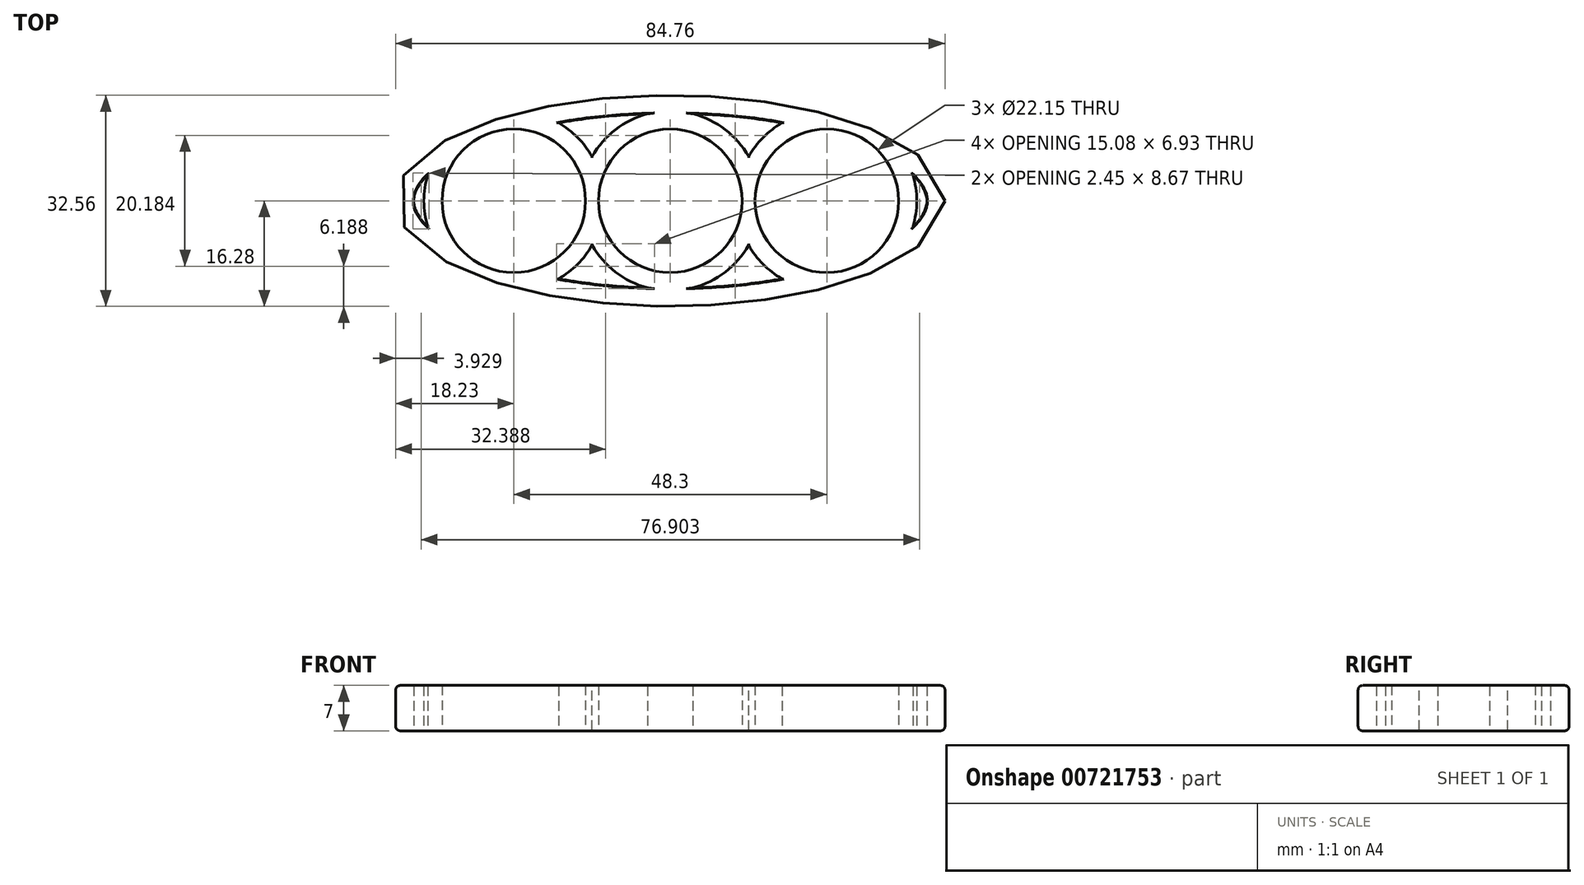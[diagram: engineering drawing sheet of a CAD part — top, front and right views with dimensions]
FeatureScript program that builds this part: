
annotation { "Feature Type Name" : "Feature", "Feature Type Description" : "" }
export const myFeature = defineFeature(function(context is Context, id is Id, definition is map)
    precondition{}
    {
        {
            var Q0;
            Q0=qCreatedBy(makeId("Top.planeOp"),FACE);
            var sketch = newSketch(context, id + "F0", { "sketchPlane" : qUnion([Q0])});
            skCircle(sketch, "E0", {"center": v(0, 0) * mm, "radius": 11.07 * mm});
            skCircle(sketch, "E1", {"center": v(24.15, 0) * mm, "radius": 11.07 * mm});
            skCircle(sketch, "E2", {"center": v(-24.15, 0) * mm, "radius": 11.07 * mm});
            skSolve(sketch);
        }
        {
            var Q0;
            Q0=qCreatedBy(makeId("Top.planeOp"),FACE);
            var sketch = newSketch(context, id + "F1", { "sketchPlane" : qUnion([Q0])});
            skEllipse(sketch, "E3", {"center": v(0, 0) * mm, "majorRadius": 42.38 * mm, "minorRadius": 16.28 * mm, "majorAxis": v(1, 0)});
            skSolve(sketch);
        }
        {
            var Q0;
            Q0=makeQuery(id+"F1.imprint","IMPRINT",FACE,{"disambiguationData":[TD([[makeQuery(id+"F1.imprint","IMPRINT",EDGE,{"derivedFrom":sQuery(id+"F1.wireOp",EDGE,"E3")}),1.0]])]});
            extrude(context, id + "F2", {"entities" : qUnion([Q0]), "depth" : 7 * mm, "offsetDistance" : 25 * mm});
        }
        {
            var Q0;
            Q0=makeQuery(id+"F0.imprint","IMPRINT",FACE,{"disambiguationData":[TD([[makeQuery(id+"F0.imprint","IMPRINT",EDGE,{"derivedFrom":sQuery(id+"F0.wireOp",EDGE,"E2")}),1.0]])]});
            var Q1;
            Q1=makeQuery(id+"F0.imprint","IMPRINT",FACE,{"disambiguationData":[TD([[makeQuery(id+"F0.imprint","IMPRINT",EDGE,{"derivedFrom":sQuery(id+"F0.wireOp",EDGE,"E0")}),1.0]])]});
            var Q2;
            Q2=makeQuery(id+"F0.imprint","IMPRINT",FACE,{"disambiguationData":[TD([[makeQuery(id+"F0.imprint","IMPRINT",EDGE,{"derivedFrom":sQuery(id+"F0.wireOp",EDGE,"E1")}),1.0]])]});
            extrude(context, id + "F3", {"entities" : qUnion([Q0, Q1, Q2]), "operationType" : NewBodyOperationType.REMOVE, "depth" : 25.5 * mm, "offsetDistance" : 25 * mm});
        }
        {
            var Q0;
            Q0=makeQuery(id+"F2.opExtrude","CAP_FACE",FACE,{"disambiguationData":[OSD([sQuery(id+"F1.wireOp",EDGE,"E3")])],"isStart":false});
            var Q1;
            Q1=makeQuery(id+"F2.opExtrude","CAP_FACE",FACE,{"disambiguationData":[OSD([sQuery(id+"F1.wireOp",EDGE,"E3")])],"isStart":true});
            shell(context, id + "F4", {"entities" : qUnion([Q0, Q1]), "thickness" : 2.8 * mm});
        }
        {
            var Q0;
            Q0=makeQuery(id+"F2.opExtrude","CAP_EDGE",EDGE,{"disambiguationData":[OSD([sQuery(id+"F1.wireOp",EDGE,"E3")])],"isStart":true});
            var Q1;
            Q1=makeQuery(id+"F2.opExtrude","CAP_EDGE",EDGE,{"disambiguationData":[OSD([sQuery(id+"F1.wireOp",EDGE,"E3")])],"isStart":false});
            fillet(context, id + "F5", {"entities" : qUnion([Q0, Q1]), "radius" : 0.7 * mm, "tangentPropagation" : true, "allowEdgeOverflow" : false});
        }
        {
            var Q0;
            {var subQ0=sQuery(id+"F1.wireOp",EDGE,"E3");Q0=makeQuery(id+"F4.opShell","OFFSET_EDGE",EDGE,{"disambiguationData":[OSD([subQ0]),TDD([makeQuery(id+"F2.opExtrude","CAP_EDGE",EDGE,{"disambiguationData":[OSD([subQ0])],"isStart":true})]),OD(1.0)]});}
            var Q1;
            Q1=makeQuery(id+"F4.opShell","OFFSET_EDGE",EDGE,{"disambiguationData":[OSD([sQuery(id+"F0.wireOp",EDGE,"E2")]),OD(0.0)]});
            var Q2;
            {var subQ0=sQuery(id+"F1.wireOp",EDGE,"E3");Q2=makeQuery(id+"F4.opShell","OFFSET_EDGE",EDGE,{"disambiguationData":[OSD([subQ0]),TDD([makeQuery(id+"F2.opExtrude","CAP_EDGE",EDGE,{"disambiguationData":[OSD([subQ0])],"isStart":true})]),OD(2.0)]});}
            var Q3;
            Q3=makeQuery(id+"F4.opShell","OFFSET_EDGE",EDGE,{"disambiguationData":[OSD([sQuery(id+"F0.wireOp",EDGE,"E2")]),OD(1.0)]});
            var Q4;
            Q4=makeQuery(id+"F4.opShell","OFFSET_EDGE",EDGE,{"disambiguationData":[OSD([sQuery(id+"F0.wireOp",EDGE,"E0")]),OD(0.0)]});
            var Q5;
            Q5=makeQuery(id+"F4.opShell","OFFSET_EDGE",EDGE,{"disambiguationData":[OSD([sQuery(id+"F0.wireOp",EDGE,"E0")]),OD(1.0)]});
            var Q6;
            {var subQ0=sQuery(id+"F1.wireOp",EDGE,"E3");Q6=makeQuery(id+"F4.opShell","OFFSET_EDGE",EDGE,{"disambiguationData":[OSD([subQ0]),TDD([makeQuery(id+"F2.opExtrude","CAP_EDGE",EDGE,{"disambiguationData":[OSD([subQ0])],"isStart":true})]),OD(3.0)]});}
            var Q7;
            Q7=makeQuery(id+"F4.opShell","OFFSET_EDGE",EDGE,{"disambiguationData":[OSD([sQuery(id+"F0.wireOp",EDGE,"E1")]),OD(1.0)]});
            var Q8;
            {var subQ0=sQuery(id+"F1.wireOp",EDGE,"E3");Q8=makeQuery(id+"F4.opShell","OFFSET_EDGE",EDGE,{"disambiguationData":[OSD([subQ0]),TDD([makeQuery(id+"F2.opExtrude","CAP_EDGE",EDGE,{"disambiguationData":[OSD([subQ0])],"isStart":true})]),OD(0.0)]});}
            var Q9;
            Q9=makeQuery(id+"F4.opShell","OFFSET_EDGE",EDGE,{"disambiguationData":[OSD([sQuery(id+"F0.wireOp",EDGE,"E1")]),OD(0.0)]});
            var Q10;
            Q10=makeQuery(id+"F4.opShell","OFFSET_EDGE",EDGE,{"disambiguationData":[OSD([sQuery(id+"F0.wireOp",EDGE,"E1")]),OD(2.0)]});
            var Q11;
            Q11=makeQuery(id+"F4.opShell","OFFSET_EDGE",EDGE,{"disambiguationData":[OSD([sQuery(id+"F0.wireOp",EDGE,"E0")]),OD(3.0)]});
            var Q12;
            {var subQ0=sQuery(id+"F1.wireOp",EDGE,"E3");Q12=makeQuery(id+"F4.opShell","OFFSET_EDGE",EDGE,{"disambiguationData":[OSD([subQ0]),TDD([makeQuery(id+"F2.opExtrude","CAP_EDGE",EDGE,{"disambiguationData":[OSD([subQ0])],"isStart":true})]),OD(5.0)]});}
            var Q13;
            Q13=makeQuery(id+"F4.opShell","OFFSET_EDGE",EDGE,{"disambiguationData":[OSD([sQuery(id+"F0.wireOp",EDGE,"E0")]),OD(2.0)]});
            var Q14;
            Q14=makeQuery(id+"F4.opShell","OFFSET_EDGE",EDGE,{"disambiguationData":[OSD([sQuery(id+"F0.wireOp",EDGE,"E2")]),OD(2.0)]});
            var Q15;
            {var subQ0=sQuery(id+"F1.wireOp",EDGE,"E3");Q15=makeQuery(id+"F4.opShell","OFFSET_EDGE",EDGE,{"disambiguationData":[OSD([subQ0]),TDD([makeQuery(id+"F2.opExtrude","CAP_EDGE",EDGE,{"disambiguationData":[OSD([subQ0])],"isStart":true})]),OD(4.0)]});}
            var Q16;
            {var subQ0=sQuery(id+"F1.wireOp",EDGE,"E3");Q16=makeQuery(id+"F4.opShell","OFFSET_EDGE",EDGE,{"disambiguationData":[OSD([subQ0]),TDD([makeQuery(id+"F2.opExtrude","CAP_EDGE",EDGE,{"disambiguationData":[OSD([subQ0])],"isStart":false})]),OD(4.0)]});}
            var Q17;
            Q17=makeQuery(id+"F4.opShell","OFFSET_EDGE",EDGE,{"disambiguationData":[OSD([sQuery(id+"F0.wireOp",EDGE,"E2"),sQuery(id+"F1.wireOp",EDGE,"E3")]),OD(2.0)]});
            var Q18;
            Q18=makeQuery(id+"F4.opShell","OFFSET_EDGE",EDGE,{"disambiguationData":[OSD([sQuery(id+"F0.wireOp",EDGE,"E0"),sQuery(id+"F1.wireOp",EDGE,"E3")]),OD(2.0)]});
            var Q19;
            {var subQ0=sQuery(id+"F1.wireOp",EDGE,"E3");Q19=makeQuery(id+"F4.opShell","OFFSET_EDGE",EDGE,{"disambiguationData":[OSD([subQ0]),TDD([makeQuery(id+"F2.opExtrude","CAP_EDGE",EDGE,{"disambiguationData":[OSD([subQ0])],"isStart":false})]),OD(5.0)]});}
            var Q20;
            Q20=makeQuery(id+"F4.opShell","OFFSET_EDGE",EDGE,{"disambiguationData":[OSD([sQuery(id+"F0.wireOp",EDGE,"E1"),sQuery(id+"F1.wireOp",EDGE,"E3")]),OD(2.0)]});
            var Q21;
            Q21=makeQuery(id+"F4.opShell","OFFSET_EDGE",EDGE,{"disambiguationData":[OSD([sQuery(id+"F0.wireOp",EDGE,"E0"),sQuery(id+"F1.wireOp",EDGE,"E3")]),OD(1.0)]});
            var Q22;
            {var subQ0=sQuery(id+"F1.wireOp",EDGE,"E3");Q22=makeQuery(id+"F4.opShell","OFFSET_EDGE",EDGE,{"disambiguationData":[OSD([subQ0]),TDD([makeQuery(id+"F2.opExtrude","CAP_EDGE",EDGE,{"disambiguationData":[OSD([subQ0])],"isStart":false})]),OD(3.0)]});}
            var Q23;
            Q23=makeQuery(id+"F4.opShell","OFFSET_EDGE",EDGE,{"disambiguationData":[OSD([sQuery(id+"F0.wireOp",EDGE,"E0"),sQuery(id+"F1.wireOp",EDGE,"E3")]),OD(0.0)]});
            var Q24;
            Q24=makeQuery(id+"F4.opShell","OFFSET_EDGE",EDGE,{"disambiguationData":[OSD([sQuery(id+"F0.wireOp",EDGE,"E2"),sQuery(id+"F1.wireOp",EDGE,"E3")]),OD(1.0)]});
            var Q25;
            {var subQ0=sQuery(id+"F1.wireOp",EDGE,"E3");Q25=makeQuery(id+"F4.opShell","OFFSET_EDGE",EDGE,{"disambiguationData":[OSD([subQ0]),TDD([makeQuery(id+"F2.opExtrude","CAP_EDGE",EDGE,{"disambiguationData":[OSD([subQ0])],"isStart":false})]),OD(2.0)]});}
            var Q26;
            Q26=makeQuery(id+"F4.opShell","OFFSET_EDGE",EDGE,{"disambiguationData":[OSD([sQuery(id+"F0.wireOp",EDGE,"E2"),sQuery(id+"F1.wireOp",EDGE,"E3")]),OD(0.0)]});
            var Q27;
            {var subQ0=sQuery(id+"F1.wireOp",EDGE,"E3");Q27=makeQuery(id+"F4.opShell","OFFSET_EDGE",EDGE,{"disambiguationData":[OSD([subQ0]),TDD([makeQuery(id+"F2.opExtrude","CAP_EDGE",EDGE,{"disambiguationData":[OSD([subQ0])],"isStart":false})]),OD(1.0)]});}
            var Q28;
            Q28=makeQuery(id+"F4.opShell","OFFSET_EDGE",EDGE,{"disambiguationData":[OSD([sQuery(id+"F0.wireOp",EDGE,"E1"),sQuery(id+"F1.wireOp",EDGE,"E3")]),OD(1.0)]});
            var Q29;
            {var subQ0=sQuery(id+"F1.wireOp",EDGE,"E3");Q29=makeQuery(id+"F4.opShell","OFFSET_EDGE",EDGE,{"disambiguationData":[OSD([subQ0]),TDD([makeQuery(id+"F2.opExtrude","CAP_EDGE",EDGE,{"disambiguationData":[OSD([subQ0])],"isStart":false})]),OD(0.0)]});}
            var Q30;
            Q30=makeQuery(id+"F4.opShell","OFFSET_EDGE",EDGE,{"disambiguationData":[OSD([sQuery(id+"F0.wireOp",EDGE,"E1"),sQuery(id+"F1.wireOp",EDGE,"E3")]),OD(0.0)]});
            fillet(context, id + "F6", {"entities" : qUnion([Q0, Q1, Q2, Q3, Q4, Q5, Q6, Q7, Q8, Q9, Q10, Q11, Q12, Q13, Q14, Q15, Q16, Q17, Q18, Q19, Q20, Q21, Q22, Q23, Q24, Q25, Q26, Q27, Q28, Q29, Q30]), "radius" : 0.1 * mm, "tangentPropagation" : true, "allowEdgeOverflow" : false});
        }
    });
